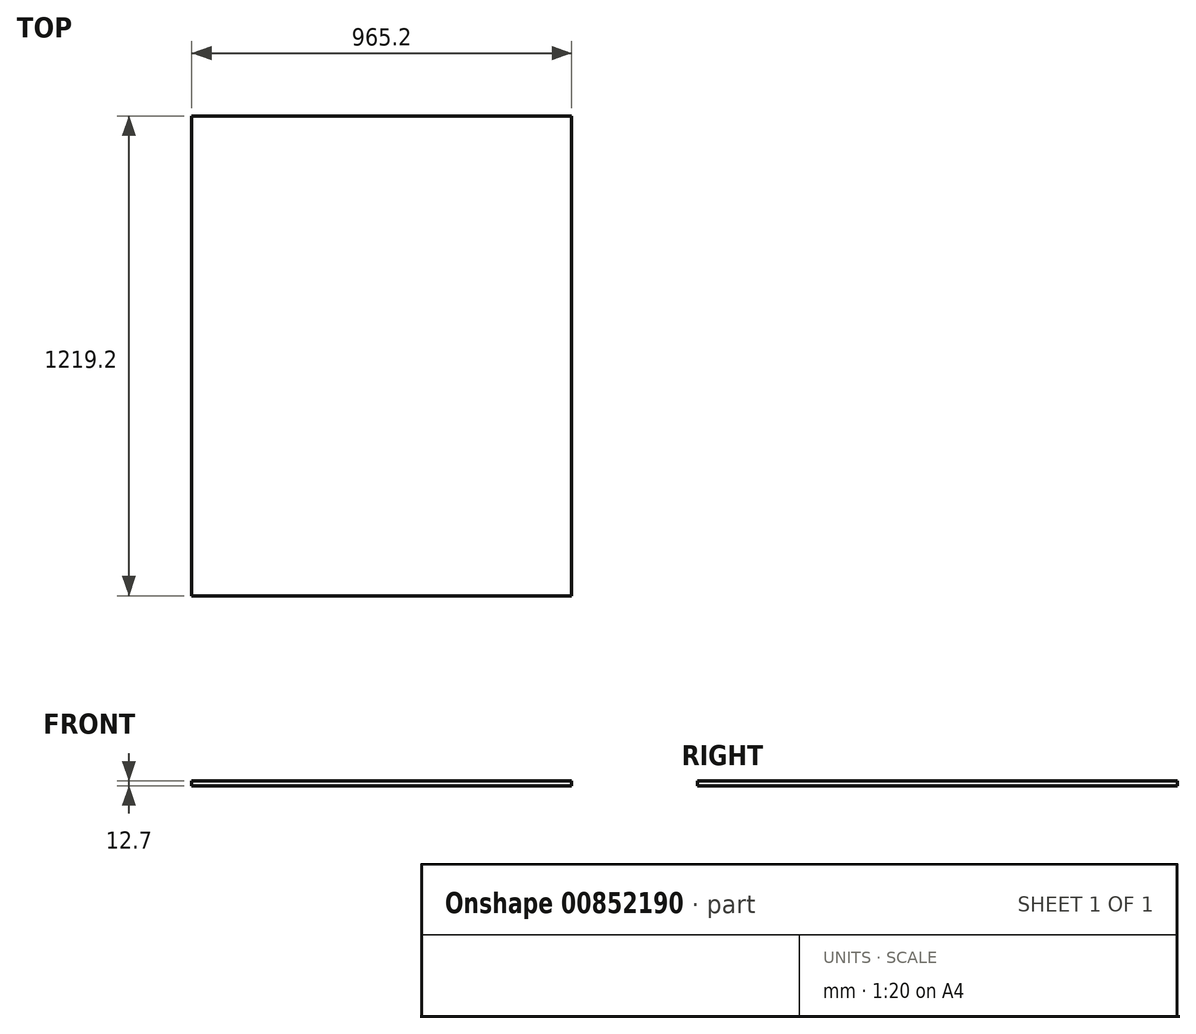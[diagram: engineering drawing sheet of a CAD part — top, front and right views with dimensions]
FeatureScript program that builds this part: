
annotation { "Feature Type Name" : "Feature", "Feature Type Description" : "" }
export const myFeature = defineFeature(function(context is Context, id is Id, definition is map)
    precondition{}
    {
        {
            var Q0;
            Q0=qCreatedBy(makeId("Top.planeOp"),FACE);
            var sketch = newSketch(context, id + "F0", { "sketchPlane" : qUnion([Q0])});
            skLineSegment(sketch, "E0.bottom", {"start": v(482.6, -609.6) * mm, "end": v(-482.6, -609.6) * mm});
            skLineSegment(sketch, "E0.top", {"start": v(482.6, 609.6) * mm, "end": v(-482.6, 609.6) * mm});
            skLineSegment(sketch, "E0.left", {"start": v(482.6, -609.6) * mm, "end": v(482.6, 609.6) * mm});
            skLineSegment(sketch, "E0.right", {"start": v(-482.6, -609.6) * mm, "end": v(-482.6, 609.6) * mm});
            skPoint(sketch, "E0.middle", {"position": v(0, 0) * mm});
            skSolve(sketch);
        }
        {
            var Q0;
            Q0=qSketchRegion(id+"F0",true);
            extrude(context, id + "F1", {"entities" : qUnion([Q0]), "depth" : 12.7 * mm, "offsetDistance" : 25.4 * mm});
        }
    });
